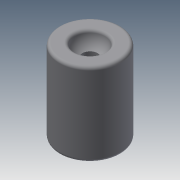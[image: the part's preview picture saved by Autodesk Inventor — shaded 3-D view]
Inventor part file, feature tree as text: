
AUTODESK INVENTOR PART (.ipt)
format: ipt  version: 2013 (Build 170138000, 138)  size: 135,680 bytes
history: native  units: mm
features: sketch x7, extrude x2, revolve x2, fillet x1
ambient origin geometry x8: Origin, YZ Plane, XZ Plane, XY Plane, X Axis, Y Axis, Z Axis, Center Point
bodies: Solid1 (feature_tree)
feature tree (12):
  extrude  "Extrusion1"  Depth=13.5mm TaperAngle=0.0deg
  extrude  "Extrusion2"  Depth=13.5mm TaperAngle=0.0deg
  sketch  "Sketch3"  dims[d6=5.0mm d7=90.0deg]
  revolve  "Revolution1"  Angle=90.0deg
  sketch  "Sketch5"
  revolve  "Revolution2"  Angle=90.0deg
  sketch  "Sketch7"
  fillet  "Fillet1"  Radius=0.5mm
  sketch  "Sketch1"  dims[d0=10.0mm d1=13.5mm d2=0.0mm]
  sketch  "Sketch2"  dims[d3=2.5mm d4=13.5mm d5=0.0mm]
  sketch  "Sketch4"  dims[d8=5.0mm d9=90.0deg d10=0.5mm]
  sketch  "Sketch6"
